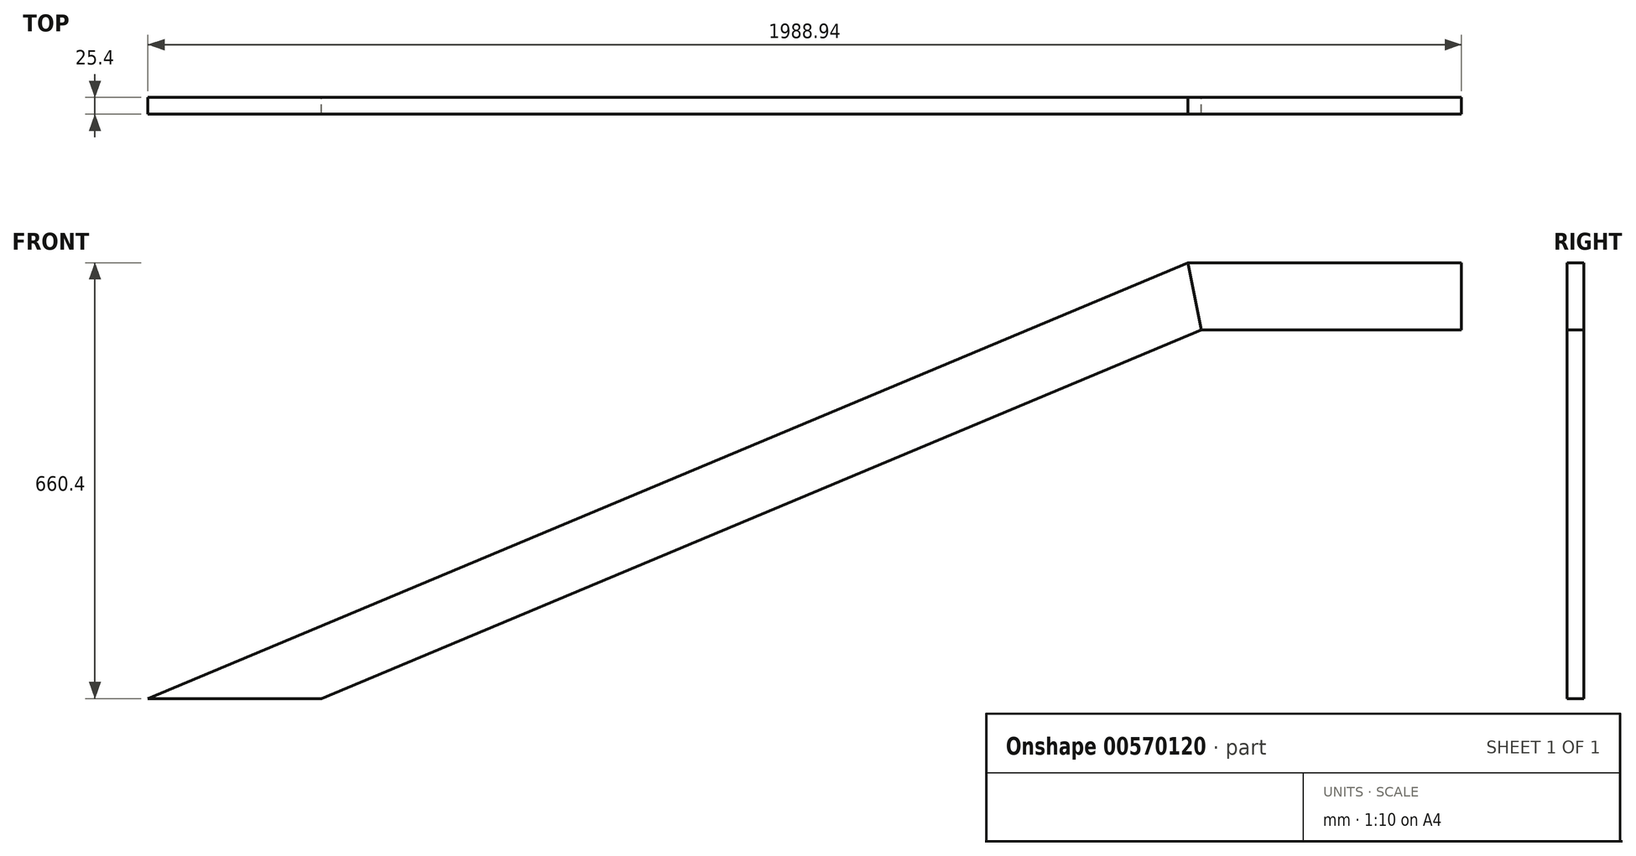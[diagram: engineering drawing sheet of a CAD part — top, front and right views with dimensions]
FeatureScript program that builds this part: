
annotation { "Feature Type Name" : "Feature", "Feature Type Description" : "" }
export const myFeature = defineFeature(function(context is Context, id is Id, definition is map)
    precondition{}
    {
        {
            var Q0;
            Q0=qCreatedBy(makeId("Front.planeOp"),FACE);
            var sketch = newSketch(context, id + "F0", { "sketchPlane" : qUnion([Q0])});
            skLineSegment(sketch, "E0", {"start": v(0, 0) * mm, "end": v(1574.8, 660.4) * mm});
            skLineSegment(sketch, "E1", {"start": v(1574.8, 660.4) * mm, "end": v(1988.94, 660.4) * mm});
            skLineSegment(sketch, "E2", {"start": v(1988.94, 660.4) * mm, "end": v(1988.94, 558.8) * mm});
            skLineSegment(sketch, "E3", {"start": v(1595.24, 558.8) * mm, "end": v(262.72, 0) * mm});
            skLineSegment(sketch, "E4", {"start": v(1988.94, 558.8) * mm, "end": v(1595.24, 558.8) * mm});
            skLineSegment(sketch, "E5", {"start": v(0, 0) * mm, "end": v(262.72, 0) * mm});
            skLineSegment(sketch, "E6", {"start": v(1574.8, 660.4) * mm, "end": v(1574.8, 0) * mm});
            skLineSegment(sketch, "E7", {"start": v(1574.8, 0) * mm, "end": v(0, 0) * mm});
            skLineSegment(sketch, "E8", {"start": v(1574.8, 660.4) * mm, "end": v(1595.24, 558.8) * mm});
            skSolve(sketch);
        }
        {
            var Q0;
            Q0=makeQuery(id+"F0.imprint","IMPRINT",FACE,{"disambiguationData":[TD([[makeQuery(id+"F0.imprint","IMPRINT",EDGE,{"derivedFrom":sQuery(id+"F0.wireOp",EDGE,"NblP0CX2-Pn9X-ETQz-nnOZ-x62gr8RrIhcG")}),1.0]])]});
            var Q1;
            {var subQ0=sQuery(id+"F0.wireOp",EDGE,"E0");Q1=makeQuery(id+"F0.imprint","IMPRINT",FACE,{"disambiguationData":[TD([[makeQuery(id+"F0.imprint","IMPRINT",EDGE,{"derivedFrom":subQ0}),-1.0]])]});}
            var Q2;
            {var subQ3=sQuery(id+"F0.wireOp",EDGE,"E8");Q2=makeQuery(id+"F0.imprint","IMPRINT",FACE,{"disambiguationData":[TD([[makeQuery(id+"F0.imprint","IMPRINT",EDGE,{"derivedFrom":subQ3}),-1.0]])]});}
            extrude(context, id + "F1", {"entities" : qUnion([Q0, Q1, Q2]), "depth" : 25.4 * mm, "offsetDistance" : 30.48 * mm});
        }
        {
            var Q0;
            Q0=makeQuery(id+"F0.imprint","IMPRINT",FACE,{"disambiguationData":[TD([[makeQuery(id+"F0.imprint","IMPRINT",EDGE,{"derivedFrom":sQuery(id+"F0.wireOp",EDGE,"E1")}),-1.0]])]});
            extrude(context, id + "F2", {"entities" : qUnion([Q0]), "depth" : 25.4 * mm, "offsetDistance" : 25.4 * mm});
        }
    });
